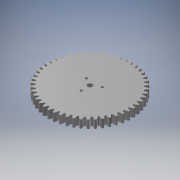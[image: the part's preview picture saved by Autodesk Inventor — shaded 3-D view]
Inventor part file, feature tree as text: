
AUTODESK INVENTOR PART (.ipt)
format: ipt  version: 2018.3 (Build 223284000, 284)  size: 353,280 bytes
history: native  units: mm (DEFAULTED — no unit token found)
features: plane x3, other x3, sketch x2, extrude x1
ambient origin geometry x8: Origin, YZ Plane, XZ Plane, XY Plane, X Axis, Y Axis, Z Axis, Center Point
bodies: Solid1 (feature_tree)
feature tree (9):
  extrude  "Extrusion1"  Depth=10.0mm TaperAngle=0.0deg
  plane  "Work Plane2"
  plane  "Work Plane8"
  plane  "Work Plane9"
  other  "Цилиндрическое зубчатое зацепление"
  sketch  "Sketch1"  dims[d0=103.833495mm d1=10.0mm d2=0.0mm]
  sketch  "Sketch2"  dims[d3=101.197967mm d4=10.0mm d5=0.0mm d16=161.916747mm d17=0.0mm d34=0.628319mm d39=0.0mm d41=0.0mm d43=161.916747mm d46=161.916747mm d47=0.0mm d48=0.0mm d49=6.0mm]
  other  "Srf1"
  other  "Средний диаметр"
